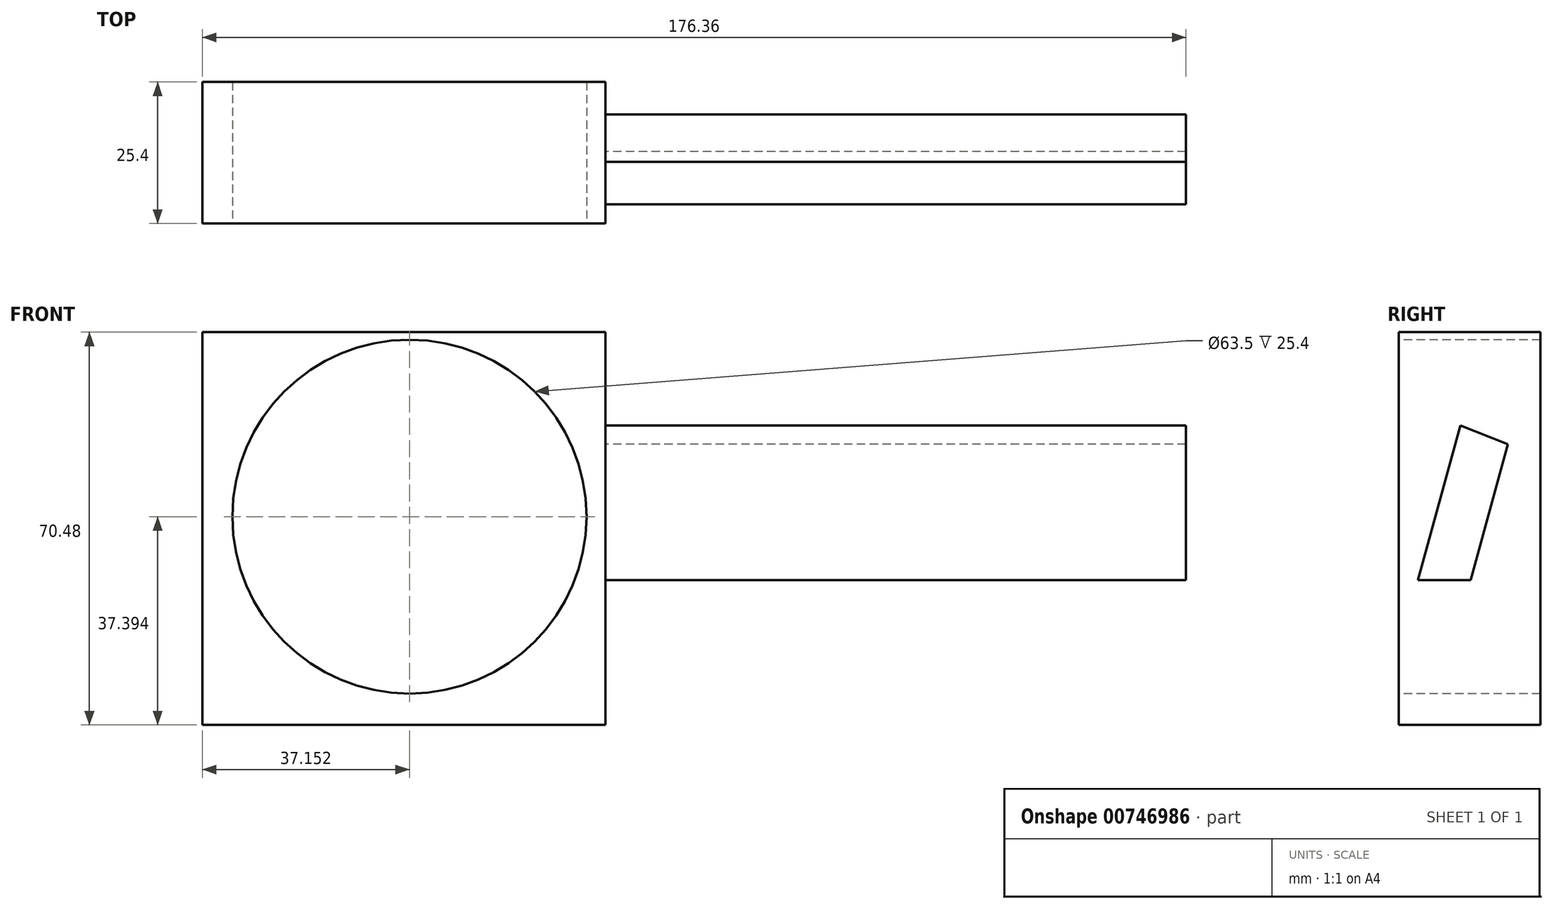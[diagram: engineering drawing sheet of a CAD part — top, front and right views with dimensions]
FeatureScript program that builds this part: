
annotation { "Feature Type Name" : "Feature", "Feature Type Description" : "" }
export const myFeature = defineFeature(function(context is Context, id is Id, definition is map)
    precondition{}
    {
        {
            var Q0;
            Q0=qCreatedBy(makeId("Front.planeOp"),FACE);
            var sketch = newSketch(context, id + "F0", { "sketchPlane" : qUnion([Q0])});
            skLineSegment(sketch, "E0.bottom", {"start": v(0, -0.67) * mm, "end": v(72.26, -0.67) * mm});
            skLineSegment(sketch, "E0.top", {"start": v(0, 69.8) * mm, "end": v(72.26, 69.8) * mm});
            skLineSegment(sketch, "E0.left", {"start": v(0, -0.67) * mm, "end": v(0, 69.8) * mm});
            skLineSegment(sketch, "E0.right", {"start": v(72.26, -0.67) * mm, "end": v(72.26, 69.8) * mm});
            skSolve(sketch);
        }
        {
            var Q0;
            Q0=makeQuery(id+"F0.imprint","IMPRINT",FACE,{"disambiguationData":[TD([[makeQuery(id+"F0.imprint","IMPRINT",EDGE,{"derivedFrom":sQuery(id+"F0.wireOp",EDGE,"E0.bottom")}),1.0]])]});
            extrude(context, id + "F1", {"entities" : qUnion([Q0]), "depth" : 25.4 * mm, "offsetDistance" : 25.4 * mm});
        }
        {
            var Q0;
            Q0=makeQuery(id+"F1.opExtrude","CAP_FACE",FACE,{"disambiguationData":[OSD([sQuery(id+"F0.wireOp",EDGE,"E0.bottom"),sQuery(id+"F0.wireOp",EDGE,"E0.top"),sQuery(id+"F0.wireOp",EDGE,"E0.left"),sQuery(id+"F0.wireOp",EDGE,"E0.right")])],"isStart":false});
            var sketch = newSketch(context, id + "F2", { "sketchPlane" : qUnion([Q0])});
            skCircle(sketch, "E1", {"center": v(37.15, 36.72) * mm, "radius": 31.75 * mm});
            skSolve(sketch);
        }
        {
            var Q0;
            Q0=makeQuery(id+"F2.imprint","IMPRINT",FACE,{"disambiguationData":[TD([[makeQuery(id+"F2.imprint","IMPRINT",EDGE,{"derivedFrom":sQuery(id+"F2.wireOp",EDGE,"E1")}),1.0]])]});
            extrude(context, id + "F3", {"entities" : qUnion([Q0]), "operationType" : NewBodyOperationType.REMOVE, "endBound" : BoundingType.THROUGH_ALL, "oppositeDirection" : true, "depth" : 25.4 * mm, "offsetDistance" : 25.4 * mm});
        }
        {
            var Q0;
            Q0=makeQuery(id+"F1.opExtrude","SWEPT_FACE",FACE,{"disambiguationData":[OSD([sQuery(id+"F0.wireOp",EDGE,"E0.right")])]});
            var sketch = newSketch(context, id + "F4", { "sketchPlane" : qUnion([Q0])});
            skLineSegment(sketch, "E2", {"start": v(-5.82, 49.72) * mm, "end": v(-12.5, 25.32) * mm});
            skLineSegment(sketch, "E3", {"start": v(-12.5, 25.32) * mm, "end": v(-21.95, 25.32) * mm});
            skLineSegment(sketch, "E4", {"start": v(-21.95, 25.32) * mm, "end": v(-14.34, 53.08) * mm});
            skLineSegment(sketch, "E5", {"start": v(-14.34, 53.08) * mm, "end": v(-5.82, 49.72) * mm});
            skSolve(sketch);
        }
        {
            var Q0;
            Q0 = qSketchRegion(id + "F4", true);
            extrude(context, id + "F5", {"entities" : qUnion([Q0]), "operationType" : NewBodyOperationType.ADD, "endBound" : BoundingType.THROUGH_ALL, "depth" : 25.4 * mm, "offsetDistance" : 25.4 * mm});
        }
    });
